# Revit family: 304_Cim795NC _-_
name_source: partatom
category: Pipe Accessories
units: mm (PartAtom-declared; Revit-internal decimal feet)

## family parameters
Always vertical = Yes
Cut with Voids When Loaded = No
Part Type = Valve - Breaks Into
Round Connector Dimension = Use Diameter
Shared = No
Work Plane-Based = No

## types (6) — shared parameters
CAT0 = Yes
Description = AUTOMATIC BALANCING VALVE - PN 25 - ACTUATOR N.C.
HH4 = 29 mm  [stored 0.0951444 ft]
HH5 = 55 mm
HH6 = 16 mm
HH7 = 44 mm  [stored 0.144357 ft]
L2D_Min = 3048 mm  [stored 10 ft]
LL4 = 11 mm  [stored 0.0360892 ft]
LL5 = 15 mm  [stored 0.0492126 ft]
LL6 = 28 mm  [stored 0.0918635 ft]
LL8 = 44 mm  [stored 0.144357 ft]
Manufacturer = Cimberio
QmdConnectorList = 301;D;302;D
URL = www.cimberio.it
magiPartTypeId = 304
magiProductFamilyId = Cim795NC *-*
zero-valued in all types: MC_Default_elevation

## per-type parameters (varying)
| type | CenSd_R1_6 | D | DD1 | DD5 | HH1 | L1 | L1__ve | L2D | LL1 | LL2 | LL3 | LL7 | R1 | W2D | magiProductId |
| Cim795NC-15 (max 600 kPa) | 11 mm  [stored 0.0360892 ft] | 15 mm | 23 mm  [stored 0.0754593 ft] | 21 mm | 29 mm  [stored 0.0951444 ft] | 12 mm  [stored 0.0393701 ft] | -12 mm  [stored -0.0393701 ft] | 105 mm | 53 mm | 81 mm  [stored 0.265748 ft] | 38 mm  [stored 0.124672 ft] | 66 mm | 13 mm | 15 mm  [stored 0.0492126 ft] | Cim795NC HF-15 |
| Cim795NC-25 (max 350 kPa) | 16 mm | 25 mm | 36 mm  [stored 0.11811 ft] | 32 mm | 33 mm | 14 mm  [stored 0.0459318 ft] | -14 mm  [stored -0.0459318 ft] | 117 mm | 59 mm  [stored 0.19357 ft] | 89 mm  [stored 0.291995 ft] | 42 mm | 68 mm | 19 mm  [stored 0.062336 ft] | 25 mm  [stored 0.082021 ft] | Cim795NC LF-25 |
| Cim795NC-20 (max 350 kPa) | 13 mm | 20 mm | 29 mm  [stored 0.0951444 ft] | 26 mm | 31 mm | 12 mm  [stored 0.0393701 ft] | -12 mm  [stored -0.0393701 ft] | 111 mm | 56 mm | 87 mm  [stored 0.285433 ft] | 39 mm  [stored 0.127953 ft] | 66 mm | 16 mm | 20 mm  [stored 0.0656168 ft] | Cim795NC LF-20 |
| Cim795NC-15 (max 350 kPa) | 11 mm  [stored 0.0360892 ft] | 15 mm | 23 mm  [stored 0.0754593 ft] | 21 mm | 29 mm  [stored 0.0951444 ft] | 12 mm  [stored 0.0393701 ft] | -12 mm  [stored -0.0393701 ft] | 105 mm | 53 mm | 81 mm  [stored 0.265748 ft] | 38 mm  [stored 0.124672 ft] | 66 mm | 13 mm | 15 mm  [stored 0.0492126 ft] | Cim795NC LF-15 |
| Cim795NC-25 (max 600 kPa) | 16 mm | 25 mm | 36 mm  [stored 0.11811 ft] | 32 mm | 33 mm | 14 mm  [stored 0.0459318 ft] | -14 mm  [stored -0.0459318 ft] | 117 mm | 59 mm  [stored 0.19357 ft] | 89 mm  [stored 0.291995 ft] | 42 mm | 68 mm | 19 mm  [stored 0.062336 ft] | 25 mm  [stored 0.082021 ft] | Cim795NC HF-25 |
| Cim795NC-20 (max 600 kPa) | 13 mm | 20 mm | 29 mm  [stored 0.0951444 ft] | 26 mm | 31 mm | 12 mm  [stored 0.0393701 ft] | -12 mm  [stored -0.0393701 ft] | 111 mm | 56 mm | 87 mm  [stored 0.285433 ft] | 39 mm  [stored 0.127953 ft] | 66 mm | 16 mm | 20 mm  [stored 0.0656168 ft] | Cim795NC HF-20 |

note: column(s) folded — value = type name in every type: magiProductCode

note: [stored X ft] marks values corroborated as IEEE doubles in the binary element streams (Revit-internal decimal feet)
